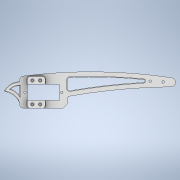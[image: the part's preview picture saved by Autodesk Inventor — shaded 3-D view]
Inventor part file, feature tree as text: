
AUTODESK INVENTOR PART (.ipt)
format: ipt  version: 2020.3 (Build 243373000, 373)  size: 421,376 bytes
history: native  units: mm
features: fillet x9, hole x4, extrude x2, sketch x1, chamfer x1
ambient origin geometry x8: Origin, YZ Plane, XZ Plane, XY Plane, X Axis, Y Axis, Z Axis, Center Point
bodies: Solid1 (feature_tree)
feature tree (17):
  sketch  "Sketch1"  dims[d4=6.0mm d5=24.6mm d6=12.4mm d7=6.0mm d15=7.0mm d17=9.0mm d21=20.0mm d23=80.0mm d24=20.0mm d29=29.670597mm d30=6.0mm d31=10.0mm d33=6.0mm d34=0.0mm d40=3.0mm d41=3.0mm d42=2.0mm d43=4.0mm d44=3.0mm d45=4.0mm d50=13.0mm d51=12.0mm d52=22.68928mm d54=1.9mm d55=50.8mm d56=4.0mm d57=2.0mm d58=90.0deg d59=8.0mm d60=20.594885mm d61=0.5mm d62=2.2mm d63=4.0mm d64=4.0mm d65=2.0mm d66=90.0deg d67=8.0mm d68=20.594885mm d69=20.92mm d70=0.0mm d71=2.0mm d80=3.0mm d81=2.0mm d82=45.0deg d87=0.5mm d88=0.5mm d89=6.8mm d90=28.4mm d99=2.9mm d100=6.0mm d101=4.0mm d102=2.0mm d103=90.0deg d104=4.3mm d105=0.0mm d107=420.0mm d108=4.0mm d109=4.0mm d110=6.0mm d111=2.0mm d112=2.0mm d113=0.5mm d114=2.1mm d115=6.0mm d116=4.0mm d117=2.0mm d118=90.0deg d119=7.3mm d120=0.0mm]
  extrude  "Extrusion1"  Depth=7.3mm
  fillet  "Fillet1"  Radius=12.4mm
  fillet  "Fillet2"  Radius=6.0mm
  fillet  "Fillet3"  Radius=7.0mm
  hole  "Hole1"  [1 undecoded]
  fillet  "Fillet4"  Radius=20.0mm
  hole  "Hole2"  [1 undecoded]
  extrude  "Extrusion3"  Depth=7.3mm
  hole  "Hole5"  [1 undecoded]
  fillet  "Fillet5"  Radius=6.0mm
  chamfer  "Chamfer2"  Distance=10.0mm
  fillet  "Fillet8"  Radius=6.0mm
  fillet  "Fillet10"  Radius=3.0mm
  fillet  "Fillet9"  Radius=3.0mm
  fillet  "Fillet11"  Radius=2.0mm
  hole  "Hole6"  [1 undecoded]
note: 4 required parameter values undecoded (feature->parameter linkage not recoverable at this tier; creation-order binding heuristic only, values carry confidence <= 0.55)
